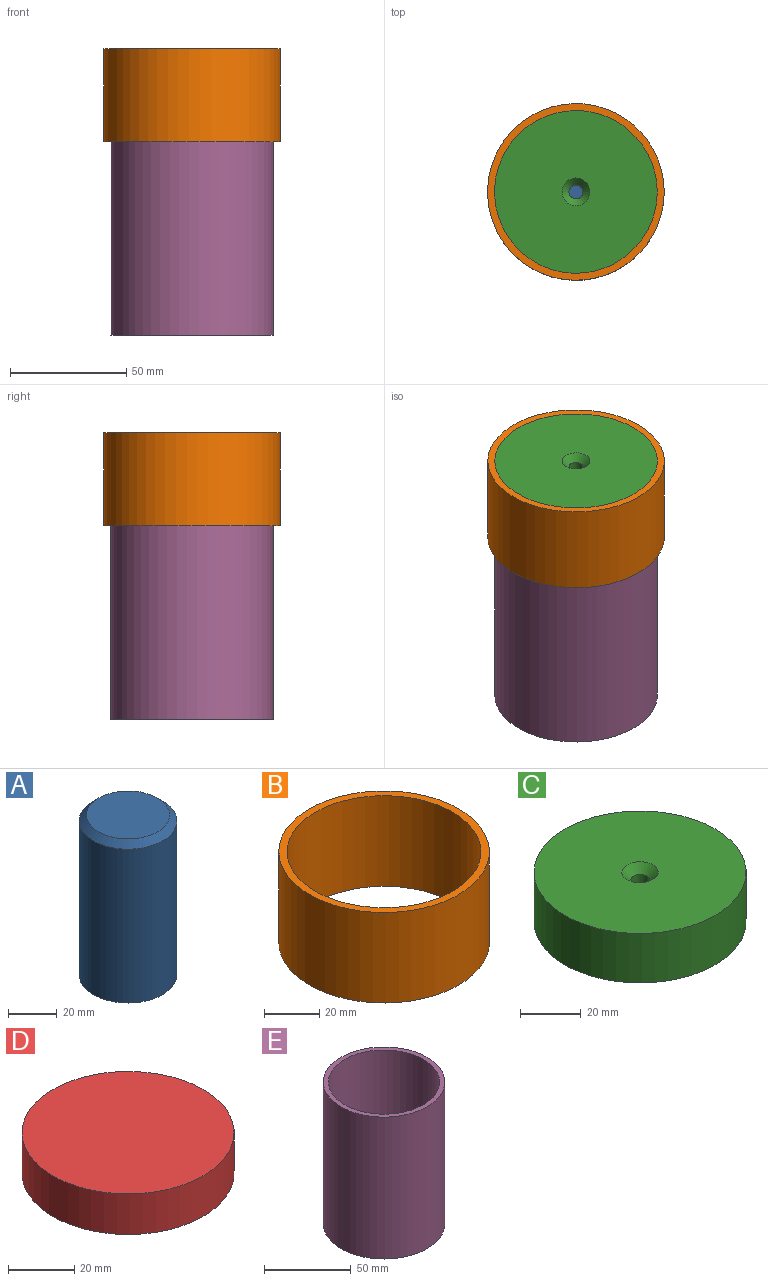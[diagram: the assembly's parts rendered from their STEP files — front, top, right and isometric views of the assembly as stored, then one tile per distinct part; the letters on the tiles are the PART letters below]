
ASSEMBLY  parts=5 mates=4
PART A: 6 faces, bbox 40x40x80 mm
  f0: cylinder r=20mm len=77mm, axis (0,0,-1), area 9676.1mm2, adj f2,f3
  f1: plane 34x34mm, normal (0,0,1), area 907.9mm2, adj f3
  f2: plane 40x40mm, normal (0,0,-1), area 1228.4mm2, adj f0,f4
  f3: cone r=17mm half-angle=45deg, axis (0,0,-1), area 493.2mm2, adj f0,f1
  f4: cylinder r=3mm len=25mm, axis (0,0,-1), area 471.2mm2, adj f2,f5
  f5: plane 6x6mm, normal (0,0,-1), area 28.3mm2, adj f4
PART B: 4 faces, bbox 76x76x40 mm
  f0: cylinder r=35mm len=70mm, axis (0,0,-1), area 8796.5mm2, adj f2,f3
  f1: cylinder r=38mm len=76mm, axis (0,0,-1), area 9550.4mm2, adj f2,f3
  f2: plane 76x76mm, normal (0,0,1), area 688mm2, adj f0,f1
  f3: plane 76x76mm, normal (0,0,-1), area 688mm2, adj f0,f1
PART C: 5 faces, bbox 70x70x20 mm
  f0: cylinder r=3mm len=17mm, axis (0,0,-1), area 320.4mm2, adj f3,f4
  f1: cylinder r=35mm len=70mm, axis (0,0,-1), area 4398.2mm2, adj f2,f3
  f2: plane 70x70mm, normal (0,0,1), area 3735.4mm2, adj f1,f4
  f3: plane 70x70mm, normal (0,0,-1), area 3820.2mm2, adj f0,f1
  f4: cone r=3mm half-angle=45deg, axis (0,0,1), area 120mm2, adj f0,f2
PART D: 3 faces, bbox 64x64x15 mm
  f0: cylinder r=32mm len=64mm, axis (0,0,-1), area 3015.9mm2, adj f1,f2
  f1: plane 64x64mm, normal (0,0,1), area 3217mm2, adj f0
  f2: plane 64x64mm, normal (0,0,-1), area 3217mm2, adj f0
PART E: 4 faces, bbox 70x70x100 mm
  f0: cylinder r=32mm len=100mm, axis (0,0,-1), area 20106.2mm2, adj f2,f3
  f1: cylinder r=35mm len=100mm, axis (0,0,-1), area 21991.1mm2, adj f2,f3
  f2: plane 70x70mm, normal (0,0,1), area 631.5mm2, adj f0,f1
  f3: plane 70x70mm, normal (0,0,-1), area 631.5mm2, adj f0,f1
PLACE A rot(axis=(1,0,0),180deg) t=(-11.7,11.56,95.88)mm
PLACE B t=(-11.7,11.56,75.88)mm
PLACE C t=(-11.7,11.56,95.88)mm
PLACE D t=(-11.7,11.56,-7.52)mm
PLACE E t=(-11.7,11.56,-7.52)mm
MATE revolute A.f0 <-> C.f1  axis (0,0,1) through (-11.7,11.56,95.88)mm
MATE revolute D.f0 <-> E.f0  axis (0,0,-1) through (-11.7,11.56,-7.52)mm
MATE revolute B.f0 <-> C.f1  axis (0,0,1) through (-11.7,11.56,115.88)mm
MATE slider C.f1 <-> E.f0  axis (0,0,-1) through (-11.7,11.56,95.88)mm
